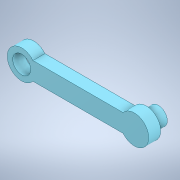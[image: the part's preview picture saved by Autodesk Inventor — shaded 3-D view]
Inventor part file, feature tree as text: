
AUTODESK INVENTOR PART (.ipt)
format: ipt  version: 2022 (Build 260153000, 153)  size: 130,048 bytes
history: native  units: in
note: dims shown in document units (in); Inventor stores cm internally (conversion verified against a paired STEP export)
features: extrude x2, sketch x1
ambient origin geometry x8: Origin, YZ Plane, XZ Plane, XY Plane, X Axis, Y Axis, Z Axis, Center Point
bodies: Solid1 (feature_tree)
feature tree (3):
  sketch  "Sketch2"  dims[d0=0.1969in d1=0.0in d2=0.1969in d3=0.0in d4=1.8504in d6=1.378in d8=0.2953in d10=0.4724in d11=0.2953in]
  extrude  "Extrusion1"  TaperAngle=0.0deg  [1 undecoded]
  extrude  "Extrusion2"  Depth=0.1969in
note: 1 required parameter value undecoded (feature->parameter linkage not recoverable at this tier; creation-order binding heuristic only, values carry confidence <= 0.55)
